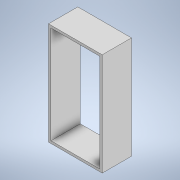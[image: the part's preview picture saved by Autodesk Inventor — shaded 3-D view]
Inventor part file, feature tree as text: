
AUTODESK INVENTOR PART (.ipt)
format: ipt  version: 2022 (Build 260153000, 153)  size: 100,352 bytes
history: native  units: in
note: dims shown in document units (in); Inventor stores cm internally (conversion verified against a paired STEP export)
features: extrude x1, sketch x1
ambient origin geometry x8: Origin, YZ Plane, XZ Plane, XY Plane, X Axis, Y Axis, Z Axis, Center Point
bodies: Solid1 (feature_tree)
feature tree (2):
  extrude  "Extrusion1"  Depth=20.0in
  sketch  "Sketch1"  dims[d0=10.0in d1=20.0in d2=11.0in d3=21.0in d4=0.5in d5=6.0in d6=0.0in]
